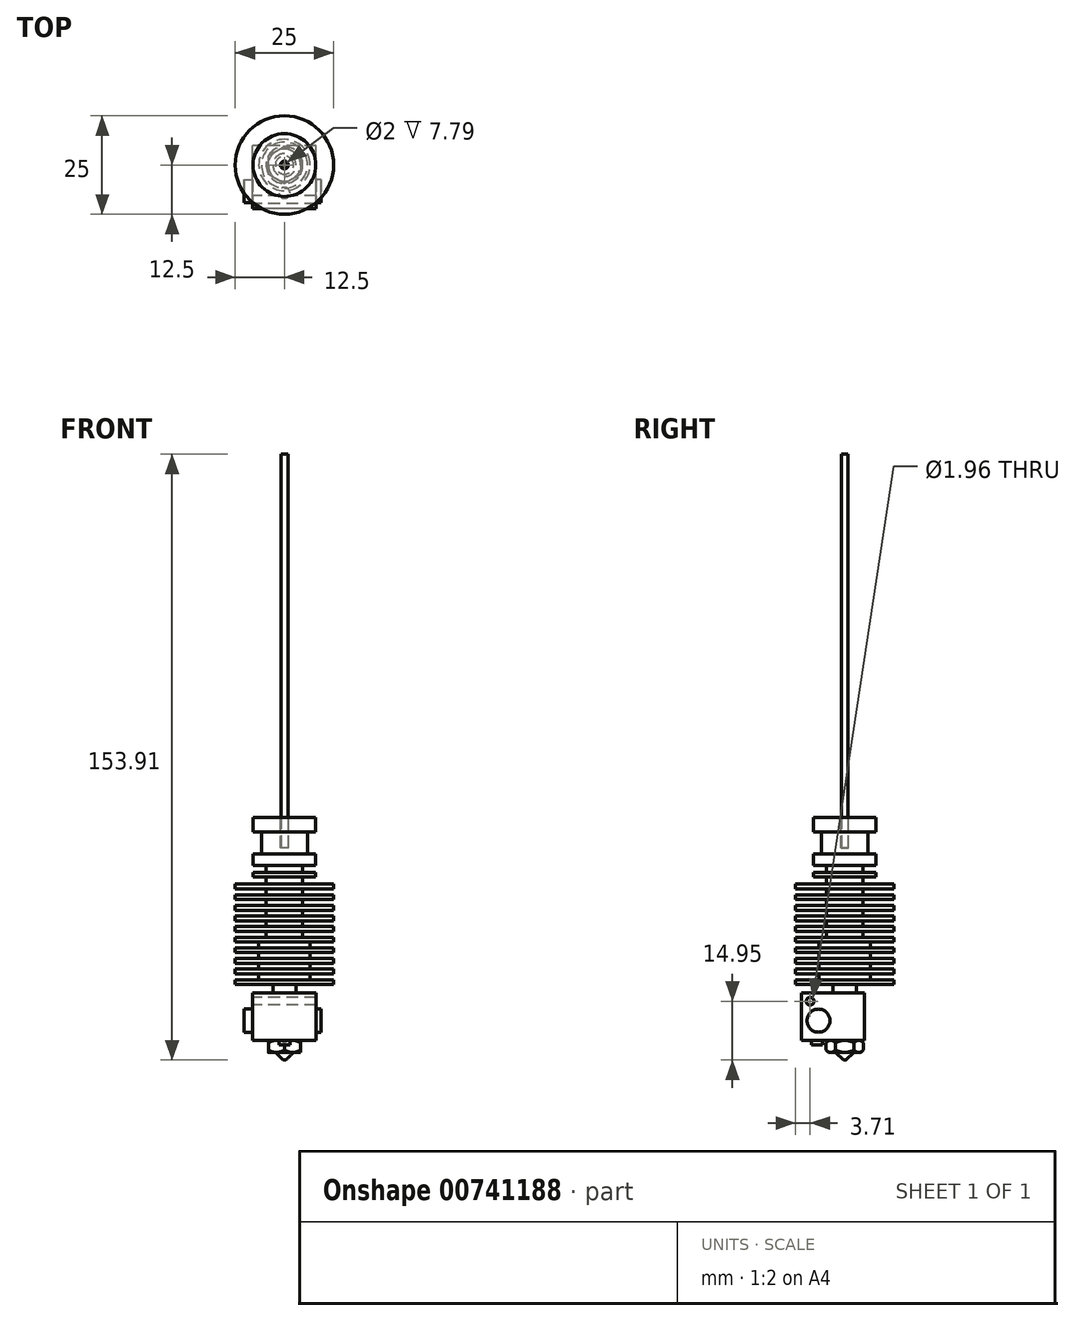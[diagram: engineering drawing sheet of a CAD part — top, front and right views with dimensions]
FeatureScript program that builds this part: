
annotation { "Feature Type Name" : "Feature", "Feature Type Description" : "" }
export const myFeature = defineFeature(function(context is Context, id is Id, definition is map)
    precondition{}
    {
        {
            var Q0;
            Q0=qCreatedBy(makeId("Front.planeOp"),FACE);
            var sketch = newSketch(context, id + "F0", { "sketchPlane" : qUnion([Q0])});
            skLineSegment(sketch, "E0", {"start": v(0, 0) * mm, "end": v(0, -61.7) * mm});
            skLineSegment(sketch, "E1", {"start": v(0, -7.79) * mm, "end": v(-1, -7.79) * mm});
            skLineSegment(sketch, "E2", {"start": v(-1, 0) * mm, "end": v(-1, -7.79) * mm});
            skLineSegment(sketch, "E3", {"start": v(-1, 0) * mm, "end": v(-7.97, 0) * mm});
            skLineSegment(sketch, "E4", {"start": v(-7.97, 0) * mm, "end": v(-7.97, -3.7) * mm});
            skLineSegment(sketch, "E5", {"start": v(-7.97, -3.7) * mm, "end": v(-5.85, -3.7) * mm});
            skLineSegment(sketch, "E6", {"start": v(-5.85, -3.7) * mm, "end": v(-5.85, -9.3) * mm});
            skLineSegment(sketch, "E7", {"start": v(-5.85, -9.3) * mm, "end": v(-7.97, -9.3) * mm});
            skLineSegment(sketch, "E8", {"start": v(-7.97, -9.3) * mm, "end": v(-7.97, -12.21) * mm});
            skLineSegment(sketch, "E9", {"start": v(-7.97, -12.21) * mm, "end": v(-4.66, -12.21) * mm});
            skLineSegment(sketch, "E10", {"start": v(-4.66, -12.21) * mm, "end": v(-4.66, -14) * mm});
            skLineSegment(sketch, "E11", {"start": v(-4.66, -15.22) * mm, "end": v(-4.66, -17) * mm});
            skLineSegment(sketch, "E12", {"start": v(-4.66, -17) * mm, "end": v(-12.5, -17) * mm});
            skLineSegment(sketch, "E13", {"start": v(-12.5, -42.5) * mm, "end": v(-2.94, -42.5) * mm});
            skLineSegment(sketch, "E14", {"start": v(-2.94, -42.5) * mm, "end": v(-2.94, -59.77) * mm});
            skLineSegment(sketch, "E15", {"start": v(-2.3, -59.77) * mm, "end": v(-2.94, -59.77) * mm});
            skLineSegment(sketch, "E16", {"start": v(-2.3, -59.77) * mm, "end": v(-0.35, -61.7) * mm});
            skLineSegment(sketch, "E17", {"start": v(-0.35, -61.7) * mm, "end": v(0, -61.7) * mm});
            skLineSegment(sketch, "E18", {"start": v(0, 0) * mm, "end": v(0, -7.79) * mm});
            skLineSegment(sketch, "E19", {"start": v(-4.66, -14) * mm, "end": v(-7.97, -14) * mm});
            skLineSegment(sketch, "E20", {"start": v(-7.97, -14) * mm, "end": v(-7.97, -15.22) * mm});
            skLineSegment(sketch, "E21", {"start": v(-7.97, -15.22) * mm, "end": v(-4.66, -15.22) * mm});
            skCircle(sketch, "E22", {"center": v(-12.5, -18.35) * mm, "radius": 1.35 * mm, "construction": true});
            skLineSegment(sketch, "E23", {"start": v(-12.5, -17) * mm, "end": v(-13.85, -17) * mm, "construction": true});
            skLineSegment(sketch, "E24", {"start": v(-13.85, -17) * mm, "end": v(-13.85, -42.5) * mm, "construction": true});
            skLineSegment(sketch, "E25", {"start": v(-13.85, -42.5) * mm, "end": v(-12.5, -42.5) * mm, "construction": true});
            skCircle(sketch, "E26", {"center": v(-12.5, -21.05) * mm, "radius": 1.35 * mm, "construction": true});
            skCircle(sketch, "E27", {"center": v(-12.5, -23.74) * mm, "radius": 1.35 * mm, "construction": true});
            skCircle(sketch, "E28", {"center": v(-12.5, -26.44) * mm, "radius": 1.35 * mm, "construction": true});
            skCircle(sketch, "E29", {"center": v(-12.5, -29.14) * mm, "radius": 1.35 * mm, "construction": true});
            skCircle(sketch, "E30", {"center": v(-12.5, -31.84) * mm, "radius": 1.35 * mm, "construction": true});
            skCircle(sketch, "E31", {"center": v(-12.5, -34.54) * mm, "radius": 1.35 * mm, "construction": true});
            skCircle(sketch, "E32", {"center": v(-12.5, -37.23) * mm, "radius": 1.35 * mm, "construction": true});
            skLineSegment(sketch, "E33", {"start": v(-12.5, -17) * mm, "end": v(-12.5, -42.5) * mm, "construction": true});
            skCircle(sketch, "E34", {"center": v(-7.97, -14.6) * mm, "radius": 2.4 * mm, "construction": true});
            skLineSegment(sketch, "E35", {"start": v(-12.5, -17) * mm, "end": v(-12.5, -18.22) * mm});
            skLineSegment(sketch, "E36", {"start": v(-12.5, -18.22) * mm, "end": v(-4.66, -18.22) * mm});
            skLineSegment(sketch, "E37", {"start": v(-4.66, -18.22) * mm, "end": v(-4.66, -19.7) * mm});
            skLineSegment(sketch, "E38", {"start": v(-4.66, -19.7) * mm, "end": v(-12.5, -19.7) * mm});
            skLineSegment(sketch, "E39", {"start": v(-13.1, -17) * mm, "end": v(-13.1, -42.5) * mm, "construction": true});
            skCircle(sketch, "E40", {"center": v(-12.5, -39.93) * mm, "radius": 1.35 * mm, "construction": true});
            skLineSegment(sketch, "E41", {"start": v(-12.5, -42.5) * mm, "end": v(-12.5, -41.28) * mm});
            skLineSegment(sketch, "E42", {"start": v(-12.5, -41.28) * mm, "end": v(-6.52, -41.28) * mm});
            skLineSegment(sketch, "E43", {"start": v(-6.52, -41.28) * mm, "end": v(-6.52, -39.8) * mm});
            skCircle(sketch, "E44", {"center": v(-12.5, -41.9) * mm, "radius": 0.61 * mm, "construction": true});
            skCircle(sketch, "E45", {"center": v(-12.5, -17.6) * mm, "radius": 0.61 * mm, "construction": true});
            skCircle(sketch, "E46", {"center": v(-12.5, -20.3) * mm, "radius": 0.61 * mm, "construction": true});
            skCircle(sketch, "E47", {"center": v(-12.5, -23) * mm, "radius": 0.61 * mm, "construction": true});
            skCircle(sketch, "E48", {"center": v(-12.5, -25.7) * mm, "radius": 0.61 * mm, "construction": true});
            skCircle(sketch, "E49", {"center": v(-12.5, -28.4) * mm, "radius": 0.61 * mm, "construction": true});
            skCircle(sketch, "E50", {"center": v(-12.5, -31.1) * mm, "radius": 0.61 * mm, "construction": true});
            skCircle(sketch, "E51", {"center": v(-12.5, -33.8) * mm, "radius": 0.61 * mm, "construction": true});
            skCircle(sketch, "E52", {"center": v(-12.5, -36.5) * mm, "radius": 0.61 * mm, "construction": true});
            skCircle(sketch, "E53", {"center": v(-12.5, -39.2) * mm, "radius": 0.61 * mm, "construction": true});
            skLineSegment(sketch, "E54", {"start": v(-6.52, -39.8) * mm, "end": v(-12.5, -39.8) * mm});
            skLineSegment(sketch, "E55", {"start": v(-12.5, -39.8) * mm, "end": v(-12.5, -38.58) * mm});
            skLineSegment(sketch, "E56", {"start": v(-12.5, -38.58) * mm, "end": v(-6.52, -38.58) * mm});
            skLineSegment(sketch, "E57", {"start": v(-6.52, -38.58) * mm, "end": v(-6.52, -37.1) * mm});
            skLineSegment(sketch, "E58", {"start": v(-6.52, -37.1) * mm, "end": v(-12.5, -37.1) * mm});
            skLineSegment(sketch, "E59", {"start": v(-12.5, -37.1) * mm, "end": v(-12.5, -35.88) * mm});
            skLineSegment(sketch, "E60", {"start": v(-12.5, -35.88) * mm, "end": v(-6.52, -35.88) * mm});
            skLineSegment(sketch, "E61", {"start": v(-12.5, -33.19) * mm, "end": v(-12.5, -34.4) * mm});
            skLineSegment(sketch, "E62", {"start": v(-12.5, -34.4) * mm, "end": v(-6.52, -34.4) * mm});
            skLineSegment(sketch, "E63", {"start": v(-6.52, -34.4) * mm, "end": v(-6.52, -35.88) * mm});
            skLineSegment(sketch, "E64", {"start": v(-12.5, -33.19) * mm, "end": v(-6.52, -33.19) * mm});
            skLineSegment(sketch, "E65", {"start": v(-6.52, -33.19) * mm, "end": v(-6.52, -31.7) * mm});
            skLineSegment(sketch, "E66", {"start": v(-6.52, -31.7) * mm, "end": v(-12.5, -31.7) * mm});
            skLineSegment(sketch, "E67", {"start": v(-12.5, -31.7) * mm, "end": v(-12.5, -30.49) * mm});
            skLineSegment(sketch, "E68", {"start": v(-12.5, -30.49) * mm, "end": v(-4.66, -30.49) * mm});
            skLineSegment(sketch, "E69", {"start": v(-4.66, -30.49) * mm, "end": v(-4.66, -29.01) * mm});
            skLineSegment(sketch, "E70", {"start": v(-4.66, -29.01) * mm, "end": v(-12.5, -29.01) * mm});
            skLineSegment(sketch, "E71", {"start": v(-12.5, -29.01) * mm, "end": v(-12.5, -27.8) * mm});
            skLineSegment(sketch, "E72", {"start": v(-12.5, -19.7) * mm, "end": v(-12.5, -20.92) * mm});
            skLineSegment(sketch, "E73", {"start": v(-12.5, -20.92) * mm, "end": v(-4.66, -20.92) * mm});
            skLineSegment(sketch, "E74", {"start": v(-4.66, -20.92) * mm, "end": v(-4.66, -22.4) * mm});
            skLineSegment(sketch, "E75", {"start": v(-4.66, -22.4) * mm, "end": v(-12.5, -22.4) * mm});
            skLineSegment(sketch, "E76", {"start": v(-12.5, -22.4) * mm, "end": v(-12.5, -23.62) * mm});
            skLineSegment(sketch, "E77", {"start": v(-12.5, -23.62) * mm, "end": v(-4.66, -23.62) * mm});
            skLineSegment(sketch, "E78", {"start": v(-4.66, -23.62) * mm, "end": v(-4.66, -25.1) * mm});
            skLineSegment(sketch, "E79", {"start": v(-4.66, -25.1) * mm, "end": v(-12.5, -25.1) * mm});
            skLineSegment(sketch, "E80", {"start": v(-12.5, -25.1) * mm, "end": v(-12.5, -26.31) * mm});
            skLineSegment(sketch, "E81", {"start": v(-12.5, -27.8) * mm, "end": v(-4.66, -27.8) * mm});
            skLineSegment(sketch, "E82", {"start": v(-4.66, -27.8) * mm, "end": v(-4.66, -26.31) * mm});
            skLineSegment(sketch, "E83", {"start": v(-4.66, -26.31) * mm, "end": v(-12.5, -26.31) * mm});
            skSolve(sketch);
        }
        {
            var Q0;
            Q0=makeQuery(id+"F0.imprint","IMPRINT",FACE,{"disambiguationData":[TD([[makeQuery(id+"F0.imprint","IMPRINT",EDGE,{"derivedFrom":sQuery(id+"F0.wireOp",EDGE,"E0")}),-1.0]])]});
            var Q1;
            Q1=sQuery(id+"F0.wireOp",EDGE,"E0");
            revolve(context, id + "F1", {"entities" : qUnion([Q0]), "axis" : qUnion([Q1]), "revolveType" : RevolveType.FULL});
        }
        {
            var Q0;
            Q0=makeQuery(id+"F1.opRevolve","SWEPT_FACE",FACE,{"disambiguationData":[OSD([sQuery(id+"F0.wireOp",EDGE,"E15")])]});
            var sketch = newSketch(context, id + "F2", { "sketchPlane" : qUnion([Q0])});
            skCircle(sketch, "E84.cCircle", {"center": v(0, 0) * mm, "radius": 4.08 * mm, "construction": true});
            skLineSegment(sketch, "E84.0", {"start": v(-4.08, -2.36) * mm, "end": v(-4.08, 2.36) * mm});
            skLineSegment(sketch, "E84.1", {"start": v(-4.08, 2.36) * mm, "end": v(0, 4.72) * mm});
            skLineSegment(sketch, "E84.2", {"start": v(0, 4.72) * mm, "end": v(4.08, 2.36) * mm});
            skLineSegment(sketch, "E84.3", {"start": v(4.08, 2.36) * mm, "end": v(4.09, -2.36) * mm});
            skLineSegment(sketch, "E84.4", {"start": v(4.09, -2.36) * mm, "end": v(0, -4.72) * mm});
            skLineSegment(sketch, "E84.5", {"start": v(0, -4.72) * mm, "end": v(-4.08, -2.36) * mm});
            skPoint(sketch, "E84.0.midPoint", {"position": v(-4.08, 0) * mm});
            skSolve(sketch);
        }
        {
            var Q0;
            Q0=qSketchRegion(id+"F2",true);
            extrude(context, id + "F3", {"entities" : qUnion([Q0]), "operationType" : NewBodyOperationType.ADD, "oppositeDirection" : true, "depth" : 3.09 * mm});
        }
        {
            var Q0;
            Q0=qCreatedBy(makeId("Front.planeOp"),FACE);
            var sketch = newSketch(context, id + "F4", { "sketchPlane" : qUnion([Q0])});
            skLineSegment(sketch, "E85.0", {"start": v(-4.08, -56.68) * mm, "end": v(-4.08, -59.77) * mm, "construction": true});
            skLineSegment(sketch, "E86", {"start": v(-4.09, -59.77) * mm, "end": v(-5.63, -58.23) * mm});
            skLineSegment(sketch, "E87", {"start": v(-5.63, -58.22) * mm, "end": v(-4.09, -56.68) * mm});
            skLineSegment(sketch, "E88", {"start": v(-5.63, -58.23) * mm, "end": v(-4.08, -58.23) * mm, "construction": true});
            skLineSegment(sketch, "E89", {"start": v(0, -63.85) * mm, "end": v(0, -68.87) * mm, "construction": true});
            skLineSegment(sketch, "E90", {"start": v(0, -63.85) * mm, "end": v(-4.09, -59.77) * mm, "construction": true});
            skLineSegment(sketch, "E91", {"start": v(-4.08, -59.77) * mm, "end": v(-4.08, -60.77) * mm});
            skLineSegment(sketch, "E92", {"start": v(-4.09, -60.77) * mm, "end": v(-7.09, -60.77) * mm});
            skLineSegment(sketch, "E93", {"start": v(-7.08, -60.77) * mm, "end": v(-7.08, -55.68) * mm});
            skLineSegment(sketch, "E94", {"start": v(-7.09, -55.68) * mm, "end": v(-4.09, -55.68) * mm});
            skLineSegment(sketch, "E95", {"start": v(-4.08, -55.68) * mm, "end": v(-4.08, -56.68) * mm});
            skSolve(sketch);
        }
        {
            var Q0;
            Q0=qSketchRegion(id+"F4",true);
            var Q1;
            Q1=sQuery(id+"F4.wireOp",EDGE,"E89");
            revolve(context, id + "F5", {"operationType" : NewBodyOperationType.REMOVE, "entities" : qUnion([Q0]), "axis" : qUnion([Q1]), "revolveType" : RevolveType.FULL, "oppositeDirection" : true});
        }
        {
            var Q0;
            Q0=makeQuery(id+"F3.opExtrude","CAP_FACE",FACE,{"disambiguationData":[OSD([sQuery(id+"F2.wireOp",EDGE,"E84.0"),sQuery(id+"F2.wireOp",EDGE,"E84.1"),sQuery(id+"F2.wireOp",EDGE,"E84.2"),sQuery(id+"F2.wireOp",EDGE,"E84.3"),sQuery(id+"F2.wireOp",EDGE,"E84.4"),sQuery(id+"F2.wireOp",EDGE,"E84.5")])],"isStart":false});
            var sketch = newSketch(context, id + "F6", { "sketchPlane" : qUnion([Q0])});
            skLineSegment(sketch, "E96", {"start": v(0, -11.04) * mm, "end": v(-8.1, -11.04) * mm});
            skLineSegment(sketch, "E97", {"start": v(-8.1, -11.04) * mm, "end": v(-8.1, 4.98) * mm});
            skLineSegment(sketch, "E98", {"start": v(-8.1, 4.98) * mm, "end": v(0, 4.98) * mm});
            skLineSegment(sketch, "E99", {"start": v(0, 4.98) * mm, "end": v(0, 0) * mm, "construction": true});
            skLineSegment(sketch, "E100", {"start": v(0, 0) * mm, "end": v(0, -11.04) * mm, "construction": true});
            skLineSegment(sketch, "E101", {"start": v(0, 4.98) * mm, "end": v(0, 12.5) * mm, "construction": true});
            skCircle(sketch, "E102.0", {"center": v(0, 0) * mm, "radius": 12.5 * mm, "construction": true});
            skLineSegment(sketch, "E103.MirrorCS", {"start": v(0, -11.04) * mm, "end": v(8.1, -11.04) * mm});
            skLineSegment(sketch, "E104.MirrorCS", {"start": v(8.1, -11.04) * mm, "end": v(8.1, 4.98) * mm});
            skLineSegment(sketch, "E105.MirrorCS", {"start": v(8.1, 4.98) * mm, "end": v(0, 4.98) * mm});
            skSolve(sketch);
        }
        {
            var Q0;
            Q0=qSketchRegion(id+"F6",true);
            extrude(context, id + "F7", {"entities" : qUnion([Q0]), "operationType" : NewBodyOperationType.ADD, "depth" : 12.02 * mm});
        }
        {
            var Q0;
            Q0=makeQuery(id+"F7.opExtrude","SWEPT_FACE",FACE,{"disambiguationData":[OSD([sQuery(id+"F6.wireOp",EDGE,"E97")])]});
            var sketch = newSketch(context, id + "F8", { "sketchPlane" : qUnion([Q0])});
            skCircle(sketch, "E106", {"center": v(6.65, -51.69) * mm, "radius": 2.92 * mm});
            skCircle(sketch, "E107", {"center": v(8.79, -46.75) * mm, "radius": 0.98 * mm});
            skSolve(sketch);
        }
        {
            var Q0;
            Q0=makeQuery(id+"F8.imprint","IMPRINT",FACE,{"disambiguationData":[TD([[makeQuery(id+"F8.imprint","IMPRINT",EDGE,{"derivedFrom":sQuery(id+"F8.wireOp",EDGE,"E107")}),1.0]])]});
            extrude(context, id + "F9", {"entities" : qUnion([Q0]), "operationType" : NewBodyOperationType.REMOVE, "endBound" : BoundingType.THROUGH_ALL, "oppositeDirection" : true, "depth" : 25 * mm});
        }
        {
            var Q0;
            Q0=makeQuery(id+"F8.imprint","IMPRINT",FACE,{"disambiguationData":[TD([[makeQuery(id+"F8.imprint","IMPRINT",EDGE,{"derivedFrom":sQuery(id+"F8.wireOp",EDGE,"E106")}),1.0]])]});
            extrude(context, id + "F10", {"entities" : qUnion([Q0]), "operationType" : NewBodyOperationType.ADD, "depth" : 2.17 * mm});
        }
        {
            var Q0;
            Q0=makeQuery(id+"F10.opExtrude","CAP_FACE",FACE,{"disambiguationData":[OSD([sQuery(id+"F8.wireOp",EDGE,"E106")])],"isStart":false});
            extrude(context, id + "F11", {"entities" : qUnion([Q0]), "operationType" : NewBodyOperationType.ADD, "oppositeDirection" : true, "depth" : 19.62 * mm});
        }
        {
            var Q0;
            Q0=makeQuery(id+"F7.opExtrude","CAP_FACE",FACE,{"disambiguationData":[OSD([sQuery(id+"F6.wireOp",EDGE,"E96"),sQuery(id+"F6.wireOp",EDGE,"E97"),sQuery(id+"F6.wireOp",EDGE,"E98"),sQuery(id+"F6.wireOp",EDGE,"E103.MirrorCS"),sQuery(id+"F6.wireOp",EDGE,"E104.MirrorCS"),sQuery(id+"F6.wireOp",EDGE,"E105.MirrorCS")])],"isStart":true});
            var sketch = newSketch(context, id + "F12", { "sketchPlane" : qUnion([Q0])});
            skLineSegment(sketch, "E108", {"start": v(0, 0) * mm, "end": v(0, 11.04) * mm, "construction": true});
            skCircle(sketch, "E109", {"center": v(0, 7.08) * mm, "radius": 1.39 * mm});
            skSolve(sketch);
        }
        {
            var Q0;
            Q0=qSketchRegion(id+"F12",true);
            extrude(context, id + "F13", {"entities" : qUnion([Q0]), "operationType" : NewBodyOperationType.ADD, "depth" : 1.12 * mm});
        }
        {
            var Q0;
            Q0=makeQuery(id+"F1.opRevolve","SWEPT_FACE",FACE,{"disambiguationData":[OSD([sQuery(id+"F0.wireOp",EDGE,"E1")])]});
            var sketch = newSketch(context, id + "F14", { "sketchPlane" : qUnion([Q0])});
            skCircle(sketch, "E110", {"center": v(0, 0) * mm, "radius": 0.88 * mm});
            skSolve(sketch);
        }
        {
            var Q0;
            Q0 = qSketchRegion(id + "F14", true);
            extrude(context, id + "F15", {"entities" : qUnion([Q0]), "depth" : 100 * mm, "offsetDistance" : 25 * mm});
        }
    });
